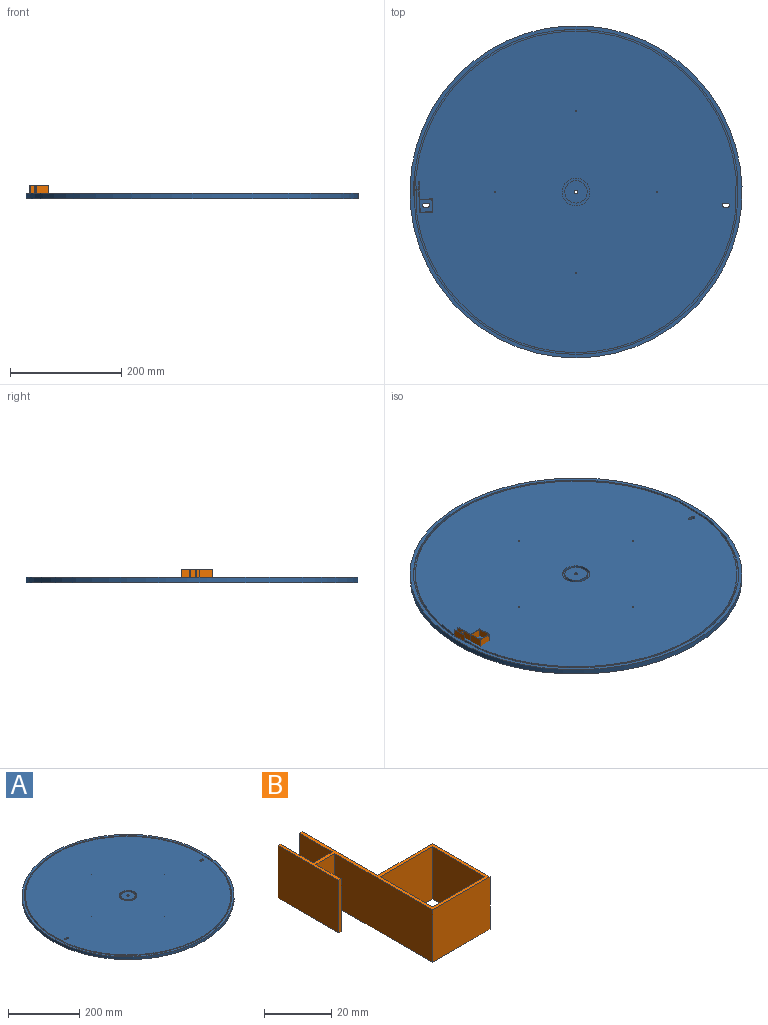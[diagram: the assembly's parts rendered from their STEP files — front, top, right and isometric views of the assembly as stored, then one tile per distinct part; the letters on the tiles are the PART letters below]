
ASSEMBLY  parts=2 mates=1
PART A: 48 faces, bbox 596.9x596.9x9.5 mm
  f0: plane 596.9x596.9mm, normal (0,0,1), area 11954.2mm2, adj f3,f13,f15,f18,f21,f24,f27,f30
  f1: plane 577.85x575.72mm, normal (0,0,1), area 259970.3mm2, adj f4,f5,f6,f7,f8,f9,f10,f11
  f2: plane 596.9x596.9mm, normal (0,0,-1), area 279641.1mm2, adj f3,f4,f5,f6,f7,f8,f9,f10
  f3: cylinder r=298.45mm len=596.9mm, axis (0,0,-1), area 17861.4mm2, adj f0,f2
  f4: plane 9.53x5.71mm, normal (0.03,-1,0), area 54.4mm2, adj f1,f2,f5,f7
  f5: cylinder r=3.49mm len=9.53mm, axis (0,0,1), area 104.5mm2, adj f1,f2,f4,f6
  f6: plane 9.53x5.71mm, normal (-0.03,1,0), area 54.4mm2, adj f1,f2,f5,f7
  f7: cylinder r=3.49mm len=9.53mm, axis (0,0,1), area 104.5mm2, adj f1,f2,f4,f6
  f8: cylinder r=3.49mm len=9.53mm, axis (0,0,1), area 104.5mm2, adj f1,f2,f9,f11
  f9: plane 9.53x5.71mm, normal (0.03,1,0), area 54.4mm2, adj f1,f2,f8,f10
  f10: cylinder r=3.49mm len=9.53mm, axis (0,0,1), area 104.5mm2, adj f1,f2,f9,f11
  f11: plane 9.53x5.71mm, normal (-0.03,-1,0), area 54.4mm2, adj f1,f2,f8,f10
  f12: plane 287.8x242.72mm, normal (0,0,1), area 1290.5mm2, adj f13,f14,f35,f38
  f13: cylinder r=292.1mm len=287.8mm, axis (0,0,1), area 1946.3mm2, adj f0,f12,f15,f36
  f14: plane 11.98x4.36mm, normal (0,0,1), area 37.2mm2, adj f12,f15,f16,f17
  f15: cylinder r=87.27mm len=11.87mm, axis (0,0,1), area 56.9mm2, adj f0,f13,f14,f18
  f16: cylinder r=84.09mm len=11.44mm, axis (0,0,1), area 54.8mm2, adj f1,f14,f19,f38
  f17: plane 55.96x5.12mm, normal (0,0,1), area 177.4mm2, adj f14,f18,f19,f20
  f18: plane 55.85x4.76mm, normal (1,0.03,0), area 266.1mm2, adj f0,f15,f17,f21
  f19: plane 55.85x4.76mm, normal (-1,-0.03,0), area 266.1mm2, adj f1,f16,f17,f22
  f20: plane 11.93x3.61mm, normal (0,0,1), area 37.2mm2, adj f17,f21,f22,f23
  f21: cylinder r=87.27mm len=11.93mm, axis (0,0,1), area 56.9mm2, adj f0,f18,f20,f24
  f22: cylinder r=84.09mm len=11.49mm, axis (0,0,1), area 54.8mm2, adj f1,f19,f20,f25
  f23: plane 581.17x262.7mm, normal (0,0,1), area 2709.7mm2, adj f20,f24,f25,f26
  f24: cylinder r=292.1mm len=581.17mm, axis (0,0,1), area 4086.8mm2, adj f0,f21,f23,f27
  f25: cylinder r=288.93mm len=574.85mm, axis (0,0,1), area 4042.3mm2, adj f1,f22,f23,f28
  f26: plane 11.93x3.61mm, normal (0,0,1), area 37.2mm2, adj f23,f27,f28,f29
  f27: cylinder r=87.27mm len=11.93mm, axis (0,0,1), area 56.9mm2, adj f0,f24,f26,f30
  f28: cylinder r=84.09mm len=11.49mm, axis (0,0,1), area 54.8mm2, adj f1,f25,f26,f31
  f29: plane 55.96x5.12mm, normal (0,0,1), area 177.4mm2, adj f26,f30,f31,f32
  f30: plane 55.85x4.76mm, normal (-1,0.03,0), area 266.1mm2, adj f0,f27,f29,f33
  f31: plane 55.85x4.76mm, normal (1,-0.03,0), area 266.1mm2, adj f1,f28,f29,f34
  f32: plane 11.98x4.36mm, normal (0,0,1), area 37.2mm2, adj f29,f33,f34,f35
  f33: cylinder r=87.27mm len=11.87mm, axis (0,0,1), area 56.9mm2, adj f0,f30,f32,f36
  f34: cylinder r=84.09mm len=11.44mm, axis (0,0,1), area 54.8mm2, adj f1,f31,f32,f37
  f35: plane 287.8x242.72mm, normal (0,0,1), area 1290.5mm2, adj f12,f32,f36,f37
  f36: cylinder r=292.1mm len=287.8mm, axis (0,0,1), area 1946.3mm2, adj f0,f13,f33,f35
  f37: cylinder r=288.93mm len=284.67mm, axis (0,0,1), area 1925.1mm2, adj f1,f34,f35,f38
  f38: cylinder r=288.93mm len=284.67mm, axis (0,0,1), area 1925.1mm2, adj f1,f12,f16,f37
  f39: cone r=0mm half-angle=45deg, axis (0,0,1), area 2.6mm2, adj f1
  f40: cone r=0mm half-angle=45deg, axis (0,0,1), area 2.6mm2, adj f1
  f41: cone r=0mm half-angle=45deg, axis (0,0,1), area 2.6mm2, adj f1
  f42: cone r=0mm half-angle=45deg, axis (0,0,1), area 2.6mm2, adj f1
  f43: cylinder r=24.89mm len=49.78mm, axis (0,0,1), area 744.9mm2, adj f1,f44
  f44: plane 49.78x49.78mm, normal (0,0,1), area 673.6mm2, adj f43,f45
  f45: cylinder r=20.13mm len=40.26mm, axis (0,0,1), area 602.3mm2, adj f44,f46
  f46: plane 40.26x40.26mm, normal (0,0,1), area 1241.3mm2, adj f45,f47
  f47: cylinder r=3.17mm len=9.53mm, axis (0,0,1), area 190mm2, adj f2,f46
PART B: 20 faces, bbox 33.1x55.9x19.1 mm
  f0: plane 55.88x33.15mm, normal (0,0,1), area 170.2mm2, adj f2,f3,f4,f5,f6,f7,f8,f9
  f1: plane 55.88x33.15mm, normal (0,0,-1), area 170.2mm2, adj f2,f3,f4,f5,f6,f7,f8,f9
  f2: plane 41.07x19.05mm, normal (-1,0,0), area 782.4mm2, adj f0,f1,f3,f15
  f3: plane 24.13x19.05mm, normal (0,-1,0), area 459.7mm2, adj f0,f1,f2,f4
  f4: plane 24.13x19.05mm, normal (1,0,0), area 459.7mm2, adj f0,f1,f3,f5
  f5: plane 23.05x19.05mm, normal (0,1,0), area 439.1mm2, adj f0,f1,f4,f6
  f6: plane 31.75x19.05mm, normal (1,0,0), area 604.8mm2, adj f0,f1,f5,f7
  f7: plane 19.05x1.08mm, normal (0,1,0), area 20.6mm2, adj f0,f1,f6,f8
  f8: plane 19.05x13.72mm, normal (-1,0,0), area 261.3mm2, adj f0,f1,f7,f9
  f9: plane 19.05x7.92mm, normal (0,1,0), area 151mm2, adj f0,f1,f8,f10
  f10: plane 19.05x13.72mm, normal (1,0,0), area 261.3mm2, adj f0,f1,f9,f11
  f11: plane 19.05x1.09mm, normal (0,1,0), area 20.8mm2, adj f0,f1,f10,f12
  f12: plane 25.4x19.05mm, normal (-1,0,0), area 483.9mm2, adj f0,f1,f11,f13
  f13: plane 19.05x1.09mm, normal (0,-1,0), area 20.8mm2, adj f0,f1,f12,f14
  f14: plane 19.05x10.59mm, normal (1,0,0), area 201.8mm2, adj f0,f1,f13,f15
  f15: plane 19.05x7.92mm, normal (0,-1,0), area 151mm2, adj f0,f1,f2,f14
  f16: plane 21.97x19.05mm, normal (-1,0,0), area 418.5mm2, adj f0,f1,f17,f19
  f17: plane 21.97x19.05mm, normal (0,-1,0), area 418.5mm2, adj f0,f1,f16,f18
  f18: plane 21.97x19.05mm, normal (1,0,0), area 418.5mm2, adj f0,f1,f17,f19
  f19: plane 21.97x19.05mm, normal (0,1,0), area 418.5mm2, adj f0,f1,f16,f18
PLACE A t=(-29.25,-18.85,-9.73)mm
PLACE B rot(axis=(0,0,1),2deg) t=(-298.73,-44.02,-5.02)mm
MATE planar B.f10 <-> A.f18  axis (1,0.03,0) through (-320,-7.78,-5.02)mm
